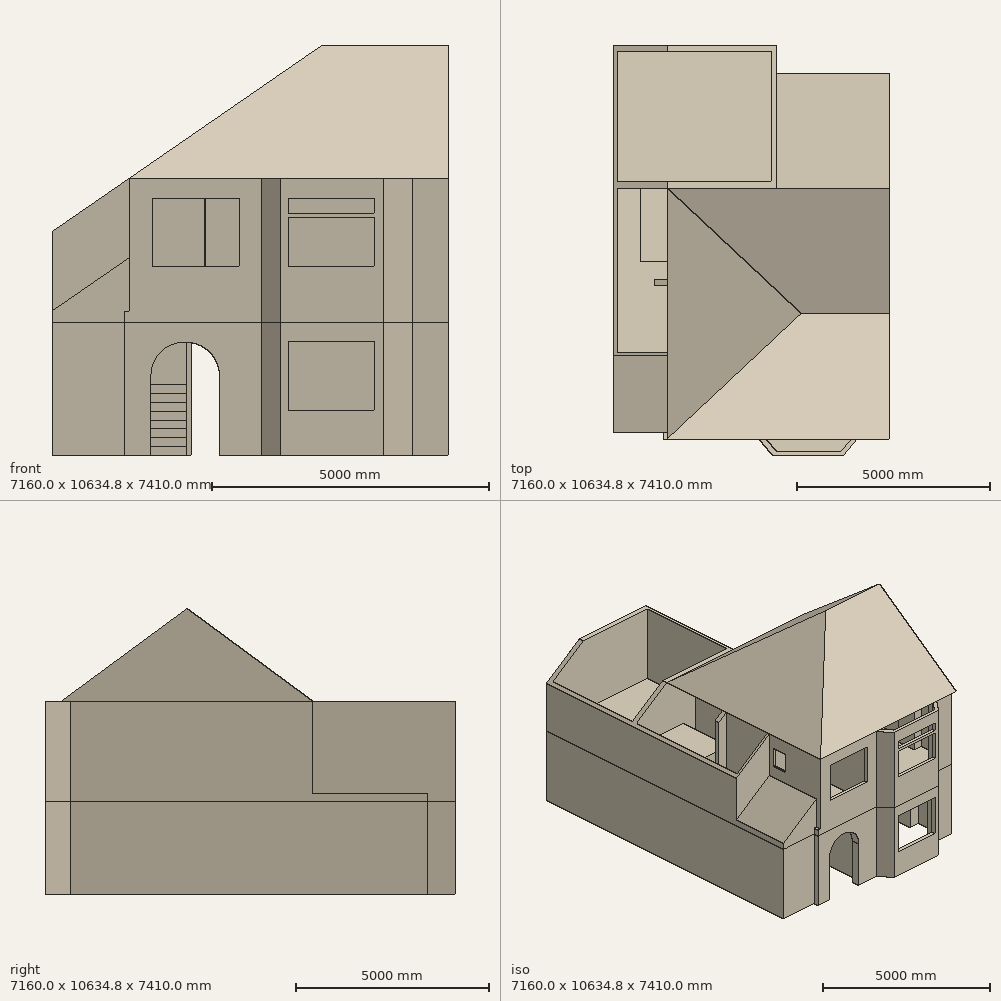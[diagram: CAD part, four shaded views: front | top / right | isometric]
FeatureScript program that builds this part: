
annotation { "Feature Type Name" : "Feature", "Feature Type Description" : "" }
export const myFeature = defineFeature(function(context is Context, id is Id, definition is map)
    precondition{}
    {
        {
            var Q0;
            Q0=qCreatedBy(makeId("Top.planeOp"),FACE);
            var sketch = newSketch(context, id + "F0", { "sketchPlane" : qUnion([Q0])});
            skLineSegment(sketch, "E0", {"start": v(2552.4, 6470.91) * mm, "end": v(2552.4, 3770.91) * mm});
            skLineSegment(sketch, "E1", {"start": v(2552.4, 2380.91) * mm, "end": v(2552.4, 1370.91) * mm});
            skLineSegment(sketch, "E2", {"start": v(2552.4, 1370.91) * mm, "end": v(-527.6, 1370.91) * mm});
            skLineSegment(sketch, "E3", {"start": v(-527.6, 2110.91) * mm, "end": v(-527.6, 1960.91) * mm});
            skLineSegment(sketch, "E4", {"start": v(-787.6, 1960.91) * mm, "end": v(-977.66, 1960.91) * mm});
            skLineSegment(sketch, "E5", {"start": v(2812.4, 6649.64) * mm, "end": v(2812.4, -1621.99) * mm});
            skLineSegment(sketch, "E6", {"start": v(-527.6, 2110.91) * mm, "end": v(-527.6, 2980.91) * mm});
            skLineSegment(sketch, "E7", {"start": v(-527.6, 2980.91) * mm, "end": v(-787.6, 2980.91) * mm});
            skLineSegment(sketch, "E8", {"start": v(-787.6, 2980.91) * mm, "end": v(-787.6, 2110.91) * mm});
            skLineSegment(sketch, "E9", {"start": v(-1127.6, -1558.17) * mm, "end": v(-1127.6, 125.16) * mm});
            skLineSegment(sketch, "E10.bottom", {"start": v(-2787.6, -689.09) * mm, "end": v(-1927.6, -689.09) * mm});
            skLineSegment(sketch, "E10.right", {"start": v(-1927.6, -689.09) * mm, "end": v(-1927.6, 1290.91) * mm});
            skLineSegment(sketch, "E11", {"start": v(-1127.6, 1033.52) * mm, "end": v(-1127.6, 692.07) * mm});
            skLineSegment(sketch, "E12", {"start": v(-1127.6, 692.07) * mm, "end": v(-977.6, 692.07) * mm});
            skLineSegment(sketch, "E13", {"start": v(-977.6, 692.07) * mm, "end": v(-977.6, 971.05) * mm});
            skLineSegment(sketch, "E14", {"start": v(-488.3, 1220.91) * mm, "end": v(2552.4, 1220.91) * mm});
            skLineSegment(sketch, "E15", {"start": v(2552.4, 1220.91) * mm, "end": v(2552.4, 220.91) * mm});
            skLineSegment(sketch, "E16", {"start": v(2552.4, 220.91) * mm, "end": v(2202.4, 220.91) * mm});
            skLineSegment(sketch, "E17", {"start": v(2202.4, 220.91) * mm, "end": v(2202.4, -488.25) * mm});
            skLineSegment(sketch, "E18", {"start": v(2202.4, -488.25) * mm, "end": v(2552.4, -488.25) * mm});
            skLineSegment(sketch, "E19", {"start": v(2552.4, -488.25) * mm, "end": v(2552.4, -1478.25) * mm});
            skLineSegment(sketch, "E20", {"start": v(2552.4, -1478.25) * mm, "end": v(1962.4, -1478.25) * mm});
            skLineSegment(sketch, "E21", {"start": v(1962.4, -1478.25) * mm, "end": v(1962.4, -1678.25) * mm});
            skLineSegment(sketch, "E22", {"start": v(1962.4, -1678.25) * mm, "end": v(1571.93, -2133.8) * mm});
            skLineSegment(sketch, "E23", {"start": v(1571.93, -2133.8) * mm, "end": v(-88.07, -2133.8) * mm});
            skLineSegment(sketch, "E24", {"start": v(-88.07, -2133.8) * mm, "end": v(-497.46, -1695.17) * mm});
            skLineSegment(sketch, "E25", {"start": v(2812.4, -1621.99) * mm, "end": v(2157.57, -1621.99) * mm});
            skLineSegment(sketch, "E26", {"start": v(2157.57, -1621.99) * mm, "end": v(1628.97, -2263.86) * mm});
            skLineSegment(sketch, "E27", {"start": v(1628.97, -2263.86) * mm, "end": v(-224.9, -2263.86) * mm});
            skLineSegment(sketch, "E28", {"start": v(-224.9, -2263.86) * mm, "end": v(-574.97, -1840.1) * mm});
            skLineSegment(sketch, "E29", {"start": v(-574.97, -1840.1) * mm, "end": v(-1127.6, -1840.1) * mm});
            skLineSegment(sketch, "E30", {"start": v(-977.6, -1684.67) * mm, "end": v(-497.46, -1695.17) * mm});
            skPoint(sketch, "E31.orphan", {"position": v(2812.4, -2479.09) * mm});
            skLineSegment(sketch, "E32", {"start": v(-1127.6, 125.16) * mm, "end": v(-977.6, 125.16) * mm});
            skLineSegment(sketch, "E33", {"start": v(-977.6, 125.16) * mm, "end": v(-977.6, -1684.67) * mm});
            skLineSegment(sketch, "E34", {"start": v(-1127.6, 1033.52) * mm, "end": v(-787.6, 1370.91) * mm});
            skLineSegment(sketch, "E35", {"start": v(-977.6, 971.05) * mm, "end": v(-725.8, 1220.91) * mm});
            skLineSegment(sketch, "E36", {"start": v(-488.3, 1220.91) * mm, "end": v(-725.8, 1220.91) * mm});
            skLineSegment(sketch, "E37", {"start": v(-1927.6, 1960.91) * mm, "end": v(-1927.6, 1890.91) * mm});
            skLineSegment(sketch, "E38", {"start": v(-3047.6, -1674.58) * mm, "end": v(-4347.6, -1674.58) * mm});
            skLineSegment(sketch, "E39", {"start": v(-4347.6, -1674.58) * mm, "end": v(-4347.6, 8370.91) * mm});
            skLineSegment(sketch, "E40", {"start": v(-4347.6, 8370.91) * mm, "end": v(-3782.36, 8370.91) * mm});
            skLineSegment(sketch, "E41", {"start": v(-5107.6, 9981.54) * mm, "end": v(-5107.6, -3919.8) * mm});
            skLineSegment(sketch, "E42", {"start": v(-527.6, 1960.91) * mm, "end": v(-527.6, 1370.91) * mm});
            skLineSegment(sketch, "E43", {"start": v(-787.6, 2110.91) * mm, "end": v(-787.6, 1370.91) * mm});
            skLineSegment(sketch, "E44", {"start": v(-1841.48, 2110.91) * mm, "end": v(-1841.48, 1960.91) * mm});
            skLineSegment(sketch, "E45", {"start": v(-977.66, 2110.91) * mm, "end": v(-977.66, 1960.91) * mm});
            skLineSegment(sketch, "E46.trimOffspring", {"start": v(-977.66, 2110.91) * mm, "end": v(-787.6, 2110.91) * mm});
            skLineSegment(sketch, "E47", {"start": v(-4047.6, 2980.91) * mm, "end": v(-4047.6, 8103.1) * mm});
            skLineSegment(sketch, "E48", {"start": v(-4047.6, 8103.1) * mm, "end": v(-3782.36, 8103.1) * mm});
            skLineSegment(sketch, "E49", {"start": v(-3782.36, 8103.1) * mm, "end": v(-3782.36, 8370.91) * mm});
            skLineSegment(sketch, "E50", {"start": v(-4047.6, 525.28) * mm, "end": v(-3047.6, 525.28) * mm});
            skLineSegment(sketch, "E51", {"start": v(-3047.6, 525.28) * mm, "end": v(-2787.6, 525.28) * mm});
            skLineSegment(sketch, "E52", {"start": v(-2787.6, 525.28) * mm, "end": v(-2787.6, 1290.91) * mm});
            skLineSegment(sketch, "E53", {"start": v(-1927.6, 1290.91) * mm, "end": v(-2787.6, 1290.91) * mm});
            skLineSegment(sketch, "E54", {"start": v(-2787.6, 1290.91) * mm, "end": v(-3047.6, 1290.91) * mm});
            skLineSegment(sketch, "E55.trimOffspring", {"start": v(-3047.6, 1290.91) * mm, "end": v(-3047.6, 525.28) * mm});
            skLineSegment(sketch, "E56.trimOffspring", {"start": v(-1927.6, 1890.91) * mm, "end": v(-1927.6, 1960.91) * mm});
            skLineSegment(sketch, "E57", {"start": v(-126.84, 8370.91) * mm, "end": v(-126.84, 7649.64) * mm});
            skLineSegment(sketch, "E58", {"start": v(-126.84, 7649.64) * mm, "end": v(2812.4, 7649.64) * mm});
            skLineSegment(sketch, "E59", {"start": v(2812.4, 7649.64) * mm, "end": v(2812.4, 6649.64) * mm});
            skLineSegment(sketch, "E60", {"start": v(2552.4, 6470.91) * mm, "end": v(2552.4, 7649.64) * mm});
            skLineSegment(sketch, "E61.bottom", {"start": v(-563.87, 8370.91) * mm, "end": v(-126.84, 8370.91) * mm});
            skLineSegment(sketch, "E61.top", {"start": v(-563.87, 8103.1) * mm, "end": v(-338.1, 8103.1) * mm});
            skLineSegment(sketch, "E61.left", {"start": v(-563.87, 8370.91) * mm, "end": v(-563.87, 8103.1) * mm});
            skLineSegment(sketch, "E61.right", {"start": v(-126.84, 8370.91) * mm, "end": v(-126.84, 8103.1) * mm});
            skLineSegment(sketch, "E62.bottom", {"start": v(-3047.6, -859.72) * mm, "end": v(-2787.6, -859.72) * mm});
            skLineSegment(sketch, "E62.top", {"start": v(-3047.6, -1558.17) * mm, "end": v(-2787.6, -1558.17) * mm});
            skLineSegment(sketch, "E63.trimOffspring", {"start": v(-3047.6, -1674.58) * mm, "end": v(-3047.6, -1840.1) * mm});
            skLineSegment(sketch, "E64.trimOffspring", {"start": v(-2787.6, -859.72) * mm, "end": v(-2787.6, 1290.91) * mm});
            skLineSegment(sketch, "E65", {"start": v(-3047.6, -1558.17) * mm, "end": v(-4047.6, -1558.17) * mm});
            skLineSegment(sketch, "E66", {"start": v(-4047.6, 525.28) * mm, "end": v(-4047.6, -1558.17) * mm});
            skLineSegment(sketch, "E67", {"start": v(2552.4, 7349.64) * mm, "end": v(-338.1, 7349.64) * mm});
            skLineSegment(sketch, "E68", {"start": v(-338.1, 7349.64) * mm, "end": v(-338.1, 8103.1) * mm});
            skLineSegment(sketch, "E69", {"start": v(2552.4, 3770.91) * mm, "end": v(2552.4, 2980.91) * mm});
            skLineSegment(sketch, "E70", {"start": v(0, 7349.64) * mm, "end": v(0, 5540.32) * mm, "construction": true});
            skLineSegment(sketch, "E71", {"start": v(0, 5540.32) * mm, "end": v(679.13, 5540.32) * mm, "construction": true});
            skLineSegment(sketch, "E72", {"start": v(679.13, 5540.32) * mm, "end": v(679.13, 7349.64) * mm, "construction": true});
            skLineSegment(sketch, "E73", {"start": v(2552.4, 4248.58) * mm, "end": v(816.18, 4248.58) * mm});
            skLineSegment(sketch, "E74", {"start": v(816.18, 4248.58) * mm, "end": v(816.18, 3608.36) * mm, "construction": true});
            skLineSegment(sketch, "E75", {"start": v(816.18, 3608.36) * mm, "end": v(2552.4, 3608.36) * mm, "construction": true});
            skLineSegment(sketch, "E76", {"start": v(-1127.6, -1840.1) * mm, "end": v(-3047.6, -1840.1) * mm});
            skLineSegment(sketch, "E77", {"start": v(-2787.6, -1558.17) * mm, "end": v(-2738.72, -1558.17) * mm});
            skLineSegment(sketch, "E78", {"start": v(-1127.6, -1558.17) * mm, "end": v(-2787.6, -1558.17) * mm});
            skLineSegment(sketch, "E79", {"start": v(1952.4, 7349.64) * mm, "end": v(1952.4, 4248.58) * mm, "construction": true});
            skLineSegment(sketch, "E80", {"start": v(-3047.6, -859.72) * mm, "end": v(-3047.6, 1290.91) * mm});
            skLineSegment(sketch, "E81.trimOffspring", {"start": v(679.13, 6634.48) * mm, "end": v(0, 6628.99) * mm});
            skLineSegment(sketch, "E82", {"start": v(1952.4, 6749.64) * mm, "end": v(679.13, 6749.64) * mm, "construction": true});
            skLineSegment(sketch, "E83", {"start": v(-4047.6, 2980.91) * mm, "end": v(-1841.48, 2980.91) * mm});
            skLineSegment(sketch, "E84", {"start": v(-1841.48, 2980.91) * mm, "end": v(-1841.48, 2110.91) * mm});
            skLineSegment(sketch, "E85", {"start": v(364.1, 2980.91) * mm, "end": v(2552.4, 2980.91) * mm});
            skPoint(sketch, "E86.start.orphan", {"position": v(-4047.6, 1960.91) * mm});
            skPoint(sketch, "E87.orphan", {"position": v(-4047.6, 2110.91) * mm});
            skLineSegment(sketch, "E88", {"start": v(-4047.6, 2980.91) * mm, "end": v(-4047.6, 525.28) * mm});
            skLineSegment(sketch, "E89", {"start": v(364.1, 2883.99) * mm, "end": v(2552.4, 2883.99) * mm});
            skLineSegment(sketch, "E90", {"start": v(-1927.6, 1960.91) * mm, "end": v(-1927.6, 2896.75) * mm});
            skLineSegment(sketch, "E91", {"start": v(-1927.6, 2896.75) * mm, "end": v(-4047.6, 2896.75) * mm});
            skLineSegment(sketch, "E92", {"start": v(-1841.48, 1960.91) * mm, "end": v(-1841.48, 1890.91) * mm});
            skLineSegment(sketch, "E93", {"start": v(-1841.48, 1890.91) * mm, "end": v(-1927.6, 1890.91) * mm});
            skLineSegment(sketch, "E94", {"start": v(-527.6, 2883.99) * mm, "end": v(-527.6, 2980.91) * mm});
            skLineSegment(sketch, "E95", {"start": v(364.1, 2883.99) * mm, "end": v(364.1, 2980.91) * mm});
            skLineSegment(sketch, "E96.trimOffspring", {"start": v(2552.4, 2883.99) * mm, "end": v(2552.4, 2380.91) * mm});
            skSolve(sketch);
        }
        {
            var Q0;
            {var subQ6=sQuery(id+"F0.wireOp",EDGE,"E1");Q0=makeQuery(id+"F0.imprint","IMPRINT",FACE,{"disambiguationData":[TD([[makeQuery(id+"F0.imprint","IMPRINT",EDGE,{"derivedFrom":subQ6}),1.0]])]});}
            var sketch = newSketch(context, id + "F1", { "sketchPlane" : qUnion([Q0])});
            skLineSegment(sketch, "E97.bottom", {"start": v(0, 7357.64) * mm, "end": v(691.93, 7357.64) * mm});
            skLineSegment(sketch, "E97.top", {"start": v(0, 5513.83) * mm, "end": v(691.93, 5513.83) * mm});
            skLineSegment(sketch, "E97.left", {"start": v(0, 7357.64) * mm, "end": v(0, 5513.83) * mm});
            skLineSegment(sketch, "E97.right", {"start": v(691.93, 7357.64) * mm, "end": v(691.93, 5513.83) * mm});
            skLineSegment(sketch, "E98.bottom", {"start": v(691.93, 6686.96) * mm, "end": v(2496.44, 6686.96) * mm});
            skLineSegment(sketch, "E98.top", {"start": v(691.93, 7229.15) * mm, "end": v(2496.44, 7229.15) * mm});
            skLineSegment(sketch, "E98.left", {"start": v(691.93, 6686.96) * mm, "end": v(691.93, 7229.15) * mm});
            skLineSegment(sketch, "E98.right", {"start": v(2496.44, 6686.96) * mm, "end": v(2496.44, 7229.15) * mm});
            skLineSegment(sketch, "E99.bottom", {"start": v(1974.66, 6686.96) * mm, "end": v(2491.44, 6686.96) * mm});
            skLineSegment(sketch, "E99.top", {"start": v(1974.66, 4299.47) * mm, "end": v(2491.44, 4299.47) * mm});
            skLineSegment(sketch, "E99.left", {"start": v(1974.66, 6686.96) * mm, "end": v(1974.66, 4299.47) * mm});
            skLineSegment(sketch, "E99.right", {"start": v(2491.44, 6686.96) * mm, "end": v(2491.44, 4299.47) * mm});
            skLineSegment(sketch, "E100.bottom", {"start": v(868.55, 4244.74) * mm, "end": v(2505.25, 4244.74) * mm});
            skLineSegment(sketch, "E100.top", {"start": v(868.55, 3653.24) * mm, "end": v(2505.25, 3653.24) * mm});
            skLineSegment(sketch, "E100.left", {"start": v(868.55, 4244.74) * mm, "end": v(868.55, 3653.24) * mm});
            skLineSegment(sketch, "E100.right", {"start": v(2505.25, 4244.74) * mm, "end": v(2505.25, 3653.24) * mm});
            skSolve(sketch);
        }
        {
            var Q0;
            Q0=makeQuery(id+"F0.imprint","IMPRINT",FACE,{"disambiguationData":[TD([[makeQuery(id+"F0.imprint","IMPRINT",EDGE,{"derivedFrom":sQuery(id+"F0.wireOp",EDGE,"E1")}),1.0]])]});
            var Q1;
            {var subQ2=sQuery(id+"F0.wireOp",EDGE,"E57");Q1=makeQuery(id+"F0.imprint","IMPRINT",FACE,{"disambiguationData":[TD([[makeQuery(id+"F0.imprint","IMPRINT",EDGE,{"derivedFrom":subQ2}),-1.0]])]});}
            var Q2;
            Q2=makeQuery(id+"F0.imprint","IMPRINT",FACE,{"disambiguationData":[TD([[makeQuery(id+"F0.imprint","IMPRINT",EDGE,{"derivedFrom":sQuery(id+"F0.wireOp",EDGE,"E44")}),-1.0]])]});
            extrude(context, id + "F2", {"entities" : qUnion([Q0, Q1, Q2]), "depth" : 2400 * mm});
        }
        {
            var Q0;
            Q0=makeQuery(id+"F2.opExtrude","SWEPT_FACE",FACE,{"disambiguationData":[OSD([sQuery(id+"F0.wireOp",EDGE,"E27")])]});
            var sketch = newSketch(context, id + "F3", { "sketchPlane" : qUnion([Q0])});
            skLineSegment(sketch, "E101.top", {"start": v(-74.9, 811.9) * mm, "end": v(1478.97, 811.9) * mm});
            skLineSegment(sketch, "E101.right", {"start": v(1478.97, 2052.8) * mm, "end": v(1478.97, 811.9) * mm});
            skLineSegment(sketch, "E102", {"start": v(-74.9, 2052.8) * mm, "end": v(-74.9, 802.64) * mm});
            skLineSegment(sketch, "E103", {"start": v(-74.9, 2052.8) * mm, "end": v(1478.97, 2052.8) * mm});
            skSolve(sketch);
        }
        {
            var Q0;
            Q0 = qSketchRegion(id + "F3", true);
            extrude(context, id + "F4", {"entities" : qUnion([Q0]), "operationType" : NewBodyOperationType.REMOVE, "oppositeDirection" : true, "depth" : 947.03 * mm});
        }
        {
            var Q0;
            Q0=makeQuery(id+"F2.opExtrude","SWEPT_FACE",FACE,{"disambiguationData":[OSD([sQuery(id+"F0.wireOp",EDGE,"E58")])]});
            var sketch = newSketch(context, id + "F5", { "sketchPlane" : qUnion([Q0])});
            skLineSegment(sketch, "E104.bottom", {"start": v(-2335.52, 1864.67) * mm, "end": v(-597.18, 1864.67) * mm});
            skLineSegment(sketch, "E104.top", {"start": v(-2335.52, 836.66) * mm, "end": v(-597.18, 836.66) * mm});
            skLineSegment(sketch, "E104.left", {"start": v(-2335.52, 1864.67) * mm, "end": v(-2335.52, 836.66) * mm});
            skLineSegment(sketch, "E104.right", {"start": v(-597.18, 1864.67) * mm, "end": v(-597.18, 836.66) * mm});
            skSolve(sketch);
        }
        {
            var Q0;
            Q0=makeQuery(id+"F5.imprint","IMPRINT",FACE,{"disambiguationData":[TD([[makeQuery(id+"F5.imprint","IMPRINT",EDGE,{"derivedFrom":sQuery(id+"F5.wireOp",EDGE,"E104.bottom")}),-1.0]])]});
            extrude(context, id + "F6", {"entities" : qUnion([Q0]), "operationType" : NewBodyOperationType.REMOVE, "oppositeDirection" : true, "depth" : 1716.48 * mm});
        }
        {
            var Q0;
            Q0=makeQuery(id+"F2.opExtrude","SWEPT_FACE",FACE,{"disambiguationData":[OSD([sQuery(id+"F0.wireOp",EDGE,"E38")])]});
            var sketch = newSketch(context, id + "F7", { "sketchPlane" : qUnion([Q0])});
            skLineSegment(sketch, "E105", {"start": v(-2567.6, 0) * mm, "end": v(-2567.6, 1430) * mm});
            skLineSegment(sketch, "E106", {"start": v(-1327.6, 0) * mm, "end": v(-1327.6, 1430) * mm});
            skArc(sketch, "E107", {"start": v(-1327.6, 1430) * mm, "mid": v(-1947.6, 2050) * mm, "end": v(-2567.6, 1430) * mm});
            skLineSegment(sketch, "E108", {"start": v(-2567.6, 0) * mm, "end": v(-1327.6, 0) * mm});
            skSolve(sketch);
        }
        {
            var Q0;
            Q0 = qSketchRegion(id + "F7", true);
            extrude(context, id + "F8", {"entities" : qUnion([Q0]), "operationType" : NewBodyOperationType.REMOVE, "depth" : 948.33 * mm});
        }
        {
            var Q0;
            Q0=makeQuery(id+"F8.boolean.opBoolean","COPY",FACE,{"derivedFrom":makeQuery(id+"F8.opExtrude","CAP_FACE",FACE,{"disambiguationData":[OSD([sQuery(id+"F7.wireOp",EDGE,"E105"),sQuery(id+"F7.wireOp",EDGE,"E106"),sQuery(id+"F7.wireOp",EDGE,"E107"),sQuery(id+"F7.wireOp",EDGE,"E108")])],"isStart":true})});
            extrude(context, id + "F9", {"entities" : qUnion([Q0]), "operationType" : NewBodyOperationType.REMOVE, "oppositeDirection" : true, "depth" : 366.27 * mm});
        }
        {
            var Q0;
            {var subQ2=sQuery(id+"F0.wireOp",EDGE,"E51");Q0=makeQuery(id+"F0.imprint","IMPRINT",FACE,{"disambiguationData":[TD([[makeQuery(id+"F0.imprint","IMPRINT",EDGE,{"derivedFrom":subQ2}),-1.0]])]});}
            var Q1;
            {var subQ2=sQuery(id+"F0.wireOp",EDGE,"E51");Q1=makeQuery(id+"F0.imprint","IMPRINT",FACE,{"disambiguationData":[TD([[makeQuery(id+"F0.imprint","IMPRINT",EDGE,{"derivedFrom":subQ2}),1.0]])]});}
            var Q2;
            {var subQ3=sQuery(id+"F0.wireOp",EDGE,"E10.bottom");Q2=makeQuery(id+"F0.imprint","IMPRINT",FACE,{"disambiguationData":[TD([[makeQuery(id+"F0.imprint","IMPRINT",EDGE,{"derivedFrom":subQ3}),1.0]])]});}
            extrude(context, id + "F10", {"entities" : qUnion([Q0, Q1, Q2]), "depth" : 2400 * mm});
        }
        {
            var Q0;
            Q0=makeQuery(id+"F10.opExtrude","SWEPT_FACE",FACE,{"disambiguationData":[OSD([sQuery(id+"F0.wireOp",EDGE,"E10.right")])]});
            var sketch = newSketch(context, id + "F11", { "sketchPlane" : qUnion([Q0])});
            skLineSegment(sketch, "E109", {"start": v(-689.09, 160) * mm, "end": v(-529.09, 160) * mm});
            skLineSegment(sketch, "E110", {"start": v(-529.09, 160) * mm, "end": v(-529.09, 320) * mm});
            skLineSegment(sketch, "E111", {"start": v(-529.09, 320) * mm, "end": v(-369.09, 320) * mm});
            skLineSegment(sketch, "E112", {"start": v(-369.09, 320) * mm, "end": v(-369.09, 480) * mm});
            skLineSegment(sketch, "E113", {"start": v(-369.09, 480) * mm, "end": v(-209.09, 480) * mm});
            skLineSegment(sketch, "E114", {"start": v(-209.09, 480) * mm, "end": v(-209.09, 640) * mm});
            skLineSegment(sketch, "E115", {"start": v(-209.09, 640) * mm, "end": v(-49.09, 640) * mm});
            skLineSegment(sketch, "E116", {"start": v(-49.09, 640) * mm, "end": v(-49.09, 800) * mm});
            skLineSegment(sketch, "E117", {"start": v(-49.09, 800) * mm, "end": v(110.91, 800) * mm});
            skLineSegment(sketch, "E118", {"start": v(110.91, 800) * mm, "end": v(110.91, 960) * mm});
            skLineSegment(sketch, "E119", {"start": v(110.91, 960) * mm, "end": v(270.91, 960) * mm});
            skLineSegment(sketch, "E120", {"start": v(270.91, 960) * mm, "end": v(270.91, 1120) * mm});
            skLineSegment(sketch, "E121", {"start": v(270.91, 1120) * mm, "end": v(430.91, 1120) * mm});
            skLineSegment(sketch, "E122", {"start": v(430.91, 1120) * mm, "end": v(430.91, 1280) * mm});
            skLineSegment(sketch, "E123", {"start": v(430.91, 1280) * mm, "end": v(597.6, 1280) * mm});
            skLineSegment(sketch, "E124", {"start": v(597.6, 1280) * mm, "end": v(1290.91, 1280) * mm});
            skLineSegment(sketch, "E125", {"start": v(-689.09, 160) * mm, "end": v(-689.09, 0) * mm});
            skLineSegment(sketch, "E126", {"start": v(-689.09, 0) * mm, "end": v(1290.91, 0) * mm});
            skLineSegment(sketch, "E127", {"start": v(1290.91, 0) * mm, "end": v(1290.91, 1280) * mm});
            skSolve(sketch);
        }
        {
            var Q0;
            {var subQ5=sQuery(id+"F11.wireOp",EDGE,"E109");Q0=makeQuery(id+"F11.imprint","IMPRINT",FACE,{"disambiguationData":[TD([[makeQuery(id+"F11.imprint","IMPRINT",EDGE,{"derivedFrom":subQ5}),1.0]])]});}
            var Q1;
            Q1=makeQuery(id+"F10.opExtrude","SWEPT_FACE",FACE,{"disambiguationData":[OSD([sQuery(id+"F0.wireOp",EDGE,"E64.trimOffspring")])]});
            extrude(context, id + "F12", {"entities" : qUnion([Q0]), "operationType" : NewBodyOperationType.REMOVE, "endBound" : BoundingType.UP_TO_SURFACE, "oppositeDirection" : true, "endBoundEntityFace" : qUnion([Q1]), "depth" : 329.84 * mm});
        }
        {
            var Q0;
            Q0=makeQuery(id+"F2.opExtrude","CAP_FACE",FACE,{"disambiguationData":[OSD([sQuery(id+"F0.wireOp",EDGE,"E0"),sQuery(id+"F0.wireOp",EDGE,"E1"),sQuery(id+"F0.wireOp",EDGE,"53525224-3efd-418c-8780-7c12f9d2bcd3"),sQuery(id+"F0.wireOp",EDGE,"E3"),sQuery(id+"F0.wireOp",EDGE,"E4"),sQuery(id+"F0.wireOp",EDGE,"E5"),sQuery(id+"F0.wireOp",EDGE,"E6"),sQuery(id+"F0.wireOp",EDGE,"E7"),sQuery(id+"F0.wireOp",EDGE,"E8"),sQuery(id+"F0.wireOp",EDGE,"E9"),sQuery(id+"F0.wireOp",EDGE,"E11"),sQuery(id+"F0.wireOp",EDGE,"E12"),sQuery(id+"F0.wireOp",EDGE,"E13"),sQuery(id+"F0.wireOp",EDGE,"E14"),sQuery(id+"F0.wireOp",EDGE,"E15"),sQuery(id+"F0.wireOp",EDGE,"E16"),sQuery(id+"F0.wireOp",EDGE,"E17"),sQuery(id+"F0.wireOp",EDGE,"E18"),sQuery(id+"F0.wireOp",EDGE,"E19"),sQuery(id+"F0.wireOp",EDGE,"E20"),sQuery(id+"F0.wireOp",EDGE,"E21"),sQuery(id+"F0.wireOp",EDGE,"E22"),sQuery(id+"F0.wireOp",EDGE,"E23"),sQuery(id+"F0.wireOp",EDGE,"E24"),sQuery(id+"F0.wireOp",EDGE,"E25"),sQuery(id+"F0.wireOp",EDGE,"E26"),sQuery(id+"F0.wireOp",EDGE,"E27"),sQuery(id+"F0.wireOp",EDGE,"E28"),sQuery(id+"F0.wireOp",EDGE,"E29"),sQuery(id+"F0.wireOp",EDGE,"E30"),sQuery(id+"F0.wireOp",EDGE,"E32"),sQuery(id+"F0.wireOp",EDGE,"E33"),sQuery(id+"F0.wireOp",EDGE,"E2"),sQuery(id+"F0.wireOp",EDGE,"E34"),sQuery(id+"F0.wireOp",EDGE,"E35"),sQuery(id+"F0.wireOp",EDGE,"E36"),sQuery(id+"F0.wireOp",EDGE,"E38"),sQuery(id+"F0.wireOp",EDGE,"E39"),sQuery(id+"F0.wireOp",EDGE,"E40"),sQuery(id+"F0.wireOp",EDGE,"E42"),sQuery(id+"F0.wireOp",EDGE,"E43"),sQuery(id+"F0.wireOp",EDGE,"E44"),sQuery(id+"F0.wireOp",EDGE,"E45"),sQuery(id+"F0.wireOp",EDGE,"E46.trimOffspring"),sQuery(id+"F0.wireOp",EDGE,"9fa25718-6e3d-4a3c-a5d5-3a83e1431973"),sQuery(id+"F0.wireOp",EDGE,"E47"),sQuery(id+"F0.wireOp",EDGE,"E48"),sQuery(id+"F0.wireOp",EDGE,"E49"),sQuery(id+"F0.wireOp",EDGE,"E86"),sQuery(id+"F0.wireOp",EDGE,"a6f443fb-dac8-401c-8383-66d9b94825dd"),sQuery(id+"F0.wireOp",EDGE,"E57"),sQuery(id+"F0.wireOp",EDGE,"E58"),sQuery(id+"F0.wireOp",EDGE,"E59"),sQuery(id+"F0.wireOp",EDGE,"E60"),sQuery(id+"F0.wireOp",EDGE,"E61.top"),sQuery(id+"F0.wireOp",EDGE,"E61.left"),sQuery(id+"F0.wireOp",EDGE,"E61.right"),sQuery(id+"F0.wireOp",EDGE,"E61.bottom"),sQuery(id+"F0.wireOp",EDGE,"E62.top"),sQuery(id+"F0.wireOp",EDGE,"E63.trimOffspring"),sQuery(id+"F0.wireOp",EDGE,"E65"),sQuery(id+"F0.wireOp",EDGE,"E66"),sQuery(id+"F0.wireOp",EDGE,"E67"),sQuery(id+"F0.wireOp",EDGE,"E68"),sQuery(id+"F0.wireOp",EDGE,"E69"),sQuery(id+"F0.wireOp",EDGE,"E76"),sQuery(id+"F0.wireOp",EDGE,"E78")])],"isStart":false});
            var sketch = newSketch(context, id + "F13", { "sketchPlane" : qUnion([Q0])});
            skLineSegment(sketch, "E128", {"start": v(-126.84, 8370.91) * mm, "end": v(-4347.6, 8370.91) * mm});
            skLineSegment(sketch, "E129", {"start": v(-4347.6, 8370.91) * mm, "end": v(-4347.6, -1674.58) * mm});
            skLineSegment(sketch, "E130", {"start": v(-4347.6, -1674.58) * mm, "end": v(-3047.6, -1674.58) * mm});
            skLineSegment(sketch, "E131", {"start": v(-3047.6, -1674.58) * mm, "end": v(-3047.6, -1840.1) * mm});
            skLineSegment(sketch, "E132", {"start": v(-3047.6, -1840.1) * mm, "end": v(-574.97, -1840.1) * mm});
            skLineSegment(sketch, "E133", {"start": v(-574.97, -1840.1) * mm, "end": v(-224.9, -2263.86) * mm});
            skLineSegment(sketch, "E134", {"start": v(-224.9, -2263.86) * mm, "end": v(1628.97, -2263.86) * mm});
            skLineSegment(sketch, "E135", {"start": v(1628.97, -2263.86) * mm, "end": v(2157.57, -1621.99) * mm});
            skLineSegment(sketch, "E136", {"start": v(2157.57, -1621.99) * mm, "end": v(2812.4, -1621.99) * mm});
            skLineSegment(sketch, "E137", {"start": v(2812.4, -1621.99) * mm, "end": v(2812.4, 7649.64) * mm});
            skLineSegment(sketch, "E138", {"start": v(2812.4, 7649.64) * mm, "end": v(-126.84, 7649.64) * mm});
            skLineSegment(sketch, "E139", {"start": v(-126.84, 7649.64) * mm, "end": v(-126.84, 8370.91) * mm});
            skSolve(sketch);
        }
        {
            var Q0;
            Q0 = qSketchRegion(id + "F13", true);
            extrude(context, id + "F14", {"entities" : qUnion([Q0]), "depth" : 210 * mm});
        }
        {
            var Q0;
            Q0=makeQuery(id+"F14.opExtrude","CAP_FACE",FACE,{"disambiguationData":[OSD([sQuery(id+"F13.wireOp",EDGE,"E128"),sQuery(id+"F13.wireOp",EDGE,"E129"),sQuery(id+"F13.wireOp",EDGE,"E130"),sQuery(id+"F13.wireOp",EDGE,"E131"),sQuery(id+"F13.wireOp",EDGE,"E132"),sQuery(id+"F13.wireOp",EDGE,"E133"),sQuery(id+"F13.wireOp",EDGE,"E134"),sQuery(id+"F13.wireOp",EDGE,"E135"),sQuery(id+"F13.wireOp",EDGE,"E136"),sQuery(id+"F13.wireOp",EDGE,"E137"),sQuery(id+"F13.wireOp",EDGE,"E138"),sQuery(id+"F13.wireOp",EDGE,"E139")])],"isStart":false});
            var sketch = newSketch(context, id + "F15", { "sketchPlane" : qUnion([Q0])});
            skLineSegment(sketch, "E140.bottom", {"start": v(-1924.03, 402.37) * mm, "end": v(-2761.06, 402.37) * mm});
            skLineSegment(sketch, "E140.top", {"start": v(-1924.03, 1956.01) * mm, "end": v(-2761.06, 1956.01) * mm});
            skLineSegment(sketch, "E140.left", {"start": v(-1924.03, 402.37) * mm, "end": v(-1924.03, 1272.66) * mm});
            skLineSegment(sketch, "E140.right", {"start": v(-2761.06, 402.37) * mm, "end": v(-2761.06, 1956.01) * mm});
            skLineSegment(sketch, "E141", {"start": v(-1924.03, 1956.01) * mm, "end": v(-1690.6, 1956.01) * mm});
            skLineSegment(sketch, "E142", {"start": v(-1690.6, 1956.01) * mm, "end": v(-1690.6, 1272.66) * mm});
            skLineSegment(sketch, "E143", {"start": v(-1690.6, 1272.66) * mm, "end": v(-1924.03, 1272.66) * mm});
            skSolve(sketch);
        }
        {
            var Q0;
            Q0=makeQuery(id+"F15.imprint","IMPRINT",FACE,{"disambiguationData":[TD([[makeQuery(id+"F15.imprint","IMPRINT",EDGE,{"derivedFrom":sQuery(id+"F15.wireOp",EDGE,"E140.bottom")}),-1.0]])]});
            extrude(context, id + "F16", {"entities" : qUnion([Q0]), "operationType" : NewBodyOperationType.REMOVE, "oppositeDirection" : true, "depth" : 244.46 * mm});
        }
        {
            var Q0;
            Q0=makeQuery(id+"F14.opExtrude","CAP_FACE",FACE,{"disambiguationData":[OSD([sQuery(id+"F13.wireOp",EDGE,"E128"),sQuery(id+"F13.wireOp",EDGE,"E129"),sQuery(id+"F13.wireOp",EDGE,"E130"),sQuery(id+"F13.wireOp",EDGE,"E131"),sQuery(id+"F13.wireOp",EDGE,"E132"),sQuery(id+"F13.wireOp",EDGE,"E133"),sQuery(id+"F13.wireOp",EDGE,"E134"),sQuery(id+"F13.wireOp",EDGE,"E135"),sQuery(id+"F13.wireOp",EDGE,"E136"),sQuery(id+"F13.wireOp",EDGE,"E137"),sQuery(id+"F13.wireOp",EDGE,"E138"),sQuery(id+"F13.wireOp",EDGE,"E139")])],"isStart":false});
            var sketch = newSketch(context, id + "F17", { "sketchPlane" : qUnion([Q0])});
            skLineSegment(sketch, "E144", {"start": v(-126.84, 8370.91) * mm, "end": v(-126.84, 4670.91) * mm});
            skLineSegment(sketch, "E145", {"start": v(-126.84, 4670.91) * mm, "end": v(2812.4, 4670.91) * mm});
            skLineSegment(sketch, "E146", {"start": v(2812.4, 4670.91) * mm, "end": v(2812.4, -1621.99) * mm});
            skLineSegment(sketch, "E147", {"start": v(2812.4, -1621.99) * mm, "end": v(2157.57, -1621.99) * mm});
            skLineSegment(sketch, "E148", {"start": v(2157.57, -1621.99) * mm, "end": v(1628.97, -2263.86) * mm});
            skLineSegment(sketch, "E149", {"start": v(1628.97, -2263.86) * mm, "end": v(-224.9, -2263.86) * mm});
            skLineSegment(sketch, "E150", {"start": v(-224.9, -2263.86) * mm, "end": v(-574.97, -1840.1) * mm});
            skLineSegment(sketch, "E151", {"start": v(-574.97, -1840.1) * mm, "end": v(-2948.68, -1840.1) * mm});
            skLineSegment(sketch, "E152", {"start": v(-4347.6, 319.79) * mm, "end": v(-4347.6, 8370.91) * mm});
            skLineSegment(sketch, "E153", {"start": v(-4347.6, 8370.91) * mm, "end": v(-126.84, 8370.91) * mm});
            skLineSegment(sketch, "E154", {"start": v(-2948.68, -1529.24) * mm, "end": v(-2948.68, -1724.11) * mm});
            skLineSegment(sketch, "E155", {"start": v(-822.49, -1724.11) * mm, "end": v(-822.49, 436.6) * mm});
            skLineSegment(sketch, "E156", {"start": v(-822.49, 1403.85) * mm, "end": v(-822.49, 1223.05) * mm});
            skLineSegment(sketch, "E157", {"start": v(-822.49, 2143.07) * mm, "end": v(-822.49, 4670.91) * mm});
            skLineSegment(sketch, "E158", {"start": v(-822.49, 4670.91) * mm, "end": v(-126.84, 4670.91) * mm});
            skLineSegment(sketch, "E159", {"start": v(2693.07, 1186.1) * mm, "end": v(2693.07, 195.2) * mm});
            skLineSegment(sketch, "E160", {"start": v(2693.07, 195.2) * mm, "end": v(2401.83, 195.2) * mm});
            skLineSegment(sketch, "E161", {"start": v(2401.83, 195.2) * mm, "end": v(2401.83, -482.62) * mm});
            skLineSegment(sketch, "E162", {"start": v(2401.83, -482.62) * mm, "end": v(2693.07, -482.62) * mm});
            skLineSegment(sketch, "E163", {"start": v(2693.07, -482.62) * mm, "end": v(2693.07, -1476.11) * mm});
            skLineSegment(sketch, "E164", {"start": v(2693.07, -1476.11) * mm, "end": v(1975.26, -1476.11) * mm});
            skLineSegment(sketch, "E165", {"start": v(1975.26, -1476.11) * mm, "end": v(1975.26, -1665.17) * mm});
            skLineSegment(sketch, "E166", {"start": v(1975.26, -1665.17) * mm, "end": v(1562.67, -2158.8) * mm});
            skLineSegment(sketch, "E167", {"start": v(1562.67, -2158.8) * mm, "end": v(-117.15, -2158.8) * mm});
            skLineSegment(sketch, "E168", {"start": v(-117.15, -2158.8) * mm, "end": v(-492.9, -1724.11) * mm});
            skLineSegment(sketch, "E169", {"start": v(-492.9, -1724.11) * mm, "end": v(-684.46, -1724.11) * mm});
            skLineSegment(sketch, "E170", {"start": v(-684.46, -1724.11) * mm, "end": v(-684.46, 436.6) * mm});
            skLineSegment(sketch, "E171", {"start": v(-684.46, 1186.1) * mm, "end": v(2693.07, 1186.1) * mm});
            skLineSegment(sketch, "E172.bottom", {"start": v(-670.17, 4522.86) * mm, "end": v(2693.07, 4522.86) * mm});
            skLineSegment(sketch, "E172.top", {"start": v(-670.17, 1354.77) * mm, "end": v(2693.07, 1354.77) * mm});
            skLineSegment(sketch, "E172.left", {"start": v(-670.17, 4522.86) * mm, "end": v(-670.17, 2143.07) * mm});
            skLineSegment(sketch, "E172.right", {"start": v(2693.07, 4522.86) * mm, "end": v(2693.07, 1354.77) * mm});
            skLineSegment(sketch, "E173.bottom", {"start": v(-4234.93, 8205.98) * mm, "end": v(-235.95, 8205.98) * mm});
            skLineSegment(sketch, "E173.top", {"start": v(-4234.93, 4840.18) * mm, "end": v(-235.95, 4840.18) * mm});
            skLineSegment(sketch, "E173.left", {"start": v(-4234.93, 8205.98) * mm, "end": v(-4234.93, 4840.18) * mm});
            skLineSegment(sketch, "E173.right", {"start": v(-235.95, 8205.98) * mm, "end": v(-235.95, 4840.18) * mm});
            skLineSegment(sketch, "E174.bottom", {"start": v(-822.49, 4670.91) * mm, "end": v(-1586.75, 4670.91) * mm});
            skLineSegment(sketch, "E174.left", {"start": v(-822.49, 4670.91) * mm, "end": v(-822.49, 2143.07) * mm});
            skLineSegment(sketch, "E174.right", {"start": v(-4234.93, 4670.91) * mm, "end": v(-4234.93, 402.37) * mm});
            skLineSegment(sketch, "E175", {"start": v(-2883.91, -1724.11) * mm, "end": v(-822.49, -1724.11) * mm});
            skLineSegment(sketch, "E176.bottom", {"start": v(-822.49, -1724.11) * mm, "end": v(-2883.91, -1724.11) * mm});
            skLineSegment(sketch, "E176.left", {"start": v(-822.49, -1724.11) * mm, "end": v(-822.49, 402.37) * mm});
            skLineSegment(sketch, "E176.right", {"start": v(-2948.68, -1724.11) * mm, "end": v(-2948.68, 319.79) * mm});
            skLineSegment(sketch, "E177.bottom", {"start": v(-2883.91, 319.79) * mm, "end": v(-1595.93, 319.79) * mm});
            skLineSegment(sketch, "E177.left", {"start": v(-2883.91, 319.79) * mm, "end": v(-2883.91, -1724.11) * mm});
            skLineSegment(sketch, "E177.right", {"start": v(-822.49, 319.79) * mm, "end": v(-822.49, -1724.11) * mm});
            skLineSegment(sketch, "E178", {"start": v(-684.46, 436.6) * mm, "end": v(-822.49, 436.6) * mm});
            skLineSegment(sketch, "E179", {"start": v(-684.46, 1186.6) * mm, "end": v(-822.49, 1186.6) * mm});
            skLineSegment(sketch, "E180", {"start": v(-670.17, 1393.07) * mm, "end": v(-822.49, 1393.07) * mm});
            skLineSegment(sketch, "E181", {"start": v(-822.49, 1393.07) * mm, "end": v(-822.49, 1403.85) * mm});
            skLineSegment(sketch, "E182", {"start": v(-822.49, 2143.07) * mm, "end": v(-670.17, 2143.07) * mm});
            skLineSegment(sketch, "E183.trimOffspring", {"start": v(-822.49, 1186.6) * mm, "end": v(-822.49, 1403.85) * mm});
            skLineSegment(sketch, "E184.trimOffspring", {"start": v(-684.46, 1186.1) * mm, "end": v(-684.46, 1186.6) * mm});
            skLineSegment(sketch, "E185.trimOffspring", {"start": v(-822.49, 436.6) * mm, "end": v(-822.49, -1529.24) * mm});
            skLineSegment(sketch, "E186.trimOffspring", {"start": v(-670.17, 1393.07) * mm, "end": v(-670.17, 1354.77) * mm});
            skLineSegment(sketch, "E187.trimOffspring", {"start": v(-822.49, 1403.85) * mm, "end": v(-822.49, 1186.6) * mm});
            skLineSegment(sketch, "E188", {"start": v(-1595.93, 402.37) * mm, "end": v(-1595.93, 319.79) * mm});
            skLineSegment(sketch, "E189", {"start": v(-1586.75, 2143.07) * mm, "end": v(-2883.91, 2143.07) * mm});
            skLineSegment(sketch, "E190", {"start": v(-2883.91, 2143.07) * mm, "end": v(-2883.91, 402.37) * mm});
            skLineSegment(sketch, "E191", {"start": v(-2948.68, 402.37) * mm, "end": v(-2948.68, 2143.07) * mm});
            skLineSegment(sketch, "E192", {"start": v(-2948.68, 2300.98) * mm, "end": v(-1714.89, 2300.98) * mm});
            skLineSegment(sketch, "E193", {"start": v(-1586.75, 2143.07) * mm, "end": v(-1586.75, 2300.98) * mm});
            skLineSegment(sketch, "E194", {"start": v(-2883.91, 402.37) * mm, "end": v(-1595.93, 402.37) * mm});
            skLineSegment(sketch, "E195.bottom", {"start": v(-2948.68, 402.37) * mm, "end": v(-4234.93, 402.37) * mm});
            skLineSegment(sketch, "E195.left", {"start": v(-2948.68, 319.79) * mm, "end": v(-2948.68, -1674.58) * mm});
            skLineSegment(sketch, "E195.right", {"start": v(-4347.6, 402.37) * mm, "end": v(-4347.6, 319.79) * mm});
            skLineSegment(sketch, "E196", {"start": v(-2606.46, 319.79) * mm, "end": v(-2883.91, 319.79) * mm});
            skLineSegment(sketch, "E197", {"start": v(-2948.68, -1024.32) * mm, "end": v(-2948.68, -1840.1) * mm});
            skLineSegment(sketch, "E198.trimOffspring", {"start": v(-2948.68, 319.79) * mm, "end": v(-4347.6, 319.79) * mm});
            skLineSegment(sketch, "E199", {"start": v(-1586.75, 2143.07) * mm, "end": v(-1586.75, 2448.43) * mm});
            skLineSegment(sketch, "E200", {"start": v(-1714.89, 4670.91) * mm, "end": v(-1714.89, 4412.16) * mm});
            skLineSegment(sketch, "E201", {"start": v(-1714.89, 2300.98) * mm, "end": v(-3271.59, 2300.98) * mm});
            skLineSegment(sketch, "E202", {"start": v(-4234.93, 2300.98) * mm, "end": v(-4234.93, 2143.07) * mm});
            skLineSegment(sketch, "E203", {"start": v(-4234.93, 2143.07) * mm, "end": v(-4021.59, 2143.07) * mm});
            skLineSegment(sketch, "E204.left", {"start": v(-4021.59, 2300.98) * mm, "end": v(-4021.59, 2143.07) * mm});
            skLineSegment(sketch, "E204.right", {"start": v(-3271.59, 2300.98) * mm, "end": v(-3271.59, 2143.07) * mm});
            skLineSegment(sketch, "E205.trimOffspring", {"start": v(-3271.59, 2143.07) * mm, "end": v(-2948.68, 2143.07) * mm});
            skLineSegment(sketch, "E206.trimOffspring", {"start": v(-4021.59, 2300.98) * mm, "end": v(-4234.93, 2300.98) * mm});
            skLineSegment(sketch, "E207.bottom", {"start": v(-4234.93, 4670.91) * mm, "end": v(-2934.93, 4670.91) * mm});
            skLineSegment(sketch, "E207.left", {"start": v(-4234.93, 4670.91) * mm, "end": v(-4234.93, 2770.91) * mm});
            skLineSegment(sketch, "E207.right", {"start": v(-2934.93, 2770.91) * mm, "end": v(-2934.93, 2751.12) * mm});
            skLineSegment(sketch, "E208.bottom", {"start": v(-3814.24, 4670.91) * mm, "end": v(-2464.24, 4670.91) * mm});
            skLineSegment(sketch, "E208.top", {"start": v(-3814.24, 2770.91) * mm, "end": v(-2464.24, 2770.91) * mm});
            skLineSegment(sketch, "E208.left", {"start": v(-3814.24, 4670.91) * mm, "end": v(-3814.24, 2770.91) * mm});
            skLineSegment(sketch, "E208.right", {"start": v(-2464.24, 4670.91) * mm, "end": v(-2464.24, 2770.91) * mm});
            skLineSegment(sketch, "E209", {"start": v(-2464.24, 2770.91) * mm, "end": v(-3814.24, 2770.91) * mm});
            skLineSegment(sketch, "E210.top", {"start": v(-2464.24, 4670.91) * mm, "end": v(-3814.24, 4670.91) * mm});
            skLineSegment(sketch, "E210.left", {"start": v(-2464.24, 2770.91) * mm, "end": v(-2464.24, 4670.91) * mm});
            skLineSegment(sketch, "E210.right", {"start": v(-3814.24, 2770.91) * mm, "end": v(-3814.24, 4670.91) * mm});
            skLineSegment(sketch, "E211.trimOffspring", {"start": v(-1714.89, 3661.58) * mm, "end": v(-1714.89, 3198.43) * mm});
            skLineSegment(sketch, "E212.trimOffspring", {"start": v(-1586.75, 4412.16) * mm, "end": v(-1586.75, 4670.91) * mm});
            skLineSegment(sketch, "E213.bottom", {"start": v(-1714.89, 2448.43) * mm, "end": v(-1586.75, 2448.43) * mm});
            skLineSegment(sketch, "E213.top", {"start": v(-1714.89, 3198.43) * mm, "end": v(-1586.75, 3198.43) * mm});
            skLineSegment(sketch, "E214.left", {"start": v(-1714.89, 3661.58) * mm, "end": v(-1714.89, 4412.16) * mm});
            skLineSegment(sketch, "E214.right", {"start": v(-1586.75, 3661.58) * mm, "end": v(-1586.75, 4412.16) * mm});
            skLineSegment(sketch, "E215.trimOffspring", {"start": v(-1714.89, 2448.43) * mm, "end": v(-1714.89, 2300.98) * mm});
            skLineSegment(sketch, "E216.trimOffspring", {"start": v(-1586.75, 3198.43) * mm, "end": v(-1586.75, 3661.58) * mm});
            skLineSegment(sketch, "E217.trimOffspring", {"start": v(-1714.89, 4670.91) * mm, "end": v(-4234.93, 4670.91) * mm});
            skSolve(sketch);
        }
        {
            var Q0;
            Q0 = qSketchRegion(id + "F17", true);
            extrude(context, id + "F18", {"entities" : qUnion([Q0]), "operationType" : NewBodyOperationType.ADD, "depth" : 2400 * mm});
        }
        {
            var Q0;
            Q0=makeQuery(id+"F18.boolean.opBoolean","SPLIT",FACE,{"disambiguationData":[TD([makeQuery(id+"F16.boolean.opBoolean","COPY",FACE,{"derivedFrom":makeQuery(id+"F16.opExtrude","SWEPT_FACE",FACE,{"disambiguationData":[OSD([sQuery(id+"F15.wireOp",EDGE,"E140.bottom")])]})})])],"derivedFrom":makeQuery(id+"F14.opExtrude","CAP_FACE",FACE,{"disambiguationData":[OSD([sQuery(id+"F13.wireOp",EDGE,"E128"),sQuery(id+"F13.wireOp",EDGE,"E129"),sQuery(id+"F13.wireOp",EDGE,"E130"),sQuery(id+"F13.wireOp",EDGE,"E131"),sQuery(id+"F13.wireOp",EDGE,"E132"),sQuery(id+"F13.wireOp",EDGE,"E133"),sQuery(id+"F13.wireOp",EDGE,"E134"),sQuery(id+"F13.wireOp",EDGE,"E135"),sQuery(id+"F13.wireOp",EDGE,"E136"),sQuery(id+"F13.wireOp",EDGE,"E137"),sQuery(id+"F13.wireOp",EDGE,"E138"),sQuery(id+"F13.wireOp",EDGE,"E139")])],"isStart":false})});
            var sketch = newSketch(context, id + "F19", { "sketchPlane" : qUnion([Q0])});
            skLineSegment(sketch, "E218.bottom", {"start": v(-3647.84, 4670.91) * mm, "end": v(-2243.86, 4670.91) * mm});
            skLineSegment(sketch, "E218.top", {"start": v(-3647.84, 2770.91) * mm, "end": v(-2243.86, 2770.91) * mm});
            skLineSegment(sketch, "E218.left", {"start": v(-3647.84, 4670.91) * mm, "end": v(-3647.84, 2770.91) * mm});
            skLineSegment(sketch, "E218.right", {"start": v(-2243.86, 4670.91) * mm, "end": v(-2243.86, 2770.91) * mm});
            skSolve(sketch);
        }
        {
            var Q0;
            Q0 = qSketchRegion(id + "F19", true);
            extrude(context, id + "F20", {"entities" : qUnion([Q0]), "operationType" : NewBodyOperationType.ADD, "depth" : 700 * mm});
        }
        {
            var Q0;
            Q0=makeQuery(id+"F18.opExtrude","CAP_FACE",FACE,{"disambiguationData":[OSD([sQuery(id+"F17.wireOp",EDGE,"E144"),sQuery(id+"F17.wireOp",EDGE,"E145"),sQuery(id+"F17.wireOp",EDGE,"E146"),sQuery(id+"F17.wireOp",EDGE,"E147"),sQuery(id+"F17.wireOp",EDGE,"E148"),sQuery(id+"F17.wireOp",EDGE,"E149"),sQuery(id+"F17.wireOp",EDGE,"E150"),sQuery(id+"F17.wireOp",EDGE,"E151"),sQuery(id+"F17.wireOp",EDGE,"E152"),sQuery(id+"F17.wireOp",EDGE,"E153"),sQuery(id+"F17.wireOp",EDGE,"E159"),sQuery(id+"F17.wireOp",EDGE,"E160"),sQuery(id+"F17.wireOp",EDGE,"E161"),sQuery(id+"F17.wireOp",EDGE,"E162"),sQuery(id+"F17.wireOp",EDGE,"E163"),sQuery(id+"F17.wireOp",EDGE,"E164"),sQuery(id+"F17.wireOp",EDGE,"E165"),sQuery(id+"F17.wireOp",EDGE,"E166"),sQuery(id+"F17.wireOp",EDGE,"E167"),sQuery(id+"F17.wireOp",EDGE,"E168"),sQuery(id+"F17.wireOp",EDGE,"E169"),sQuery(id+"F17.wireOp",EDGE,"E170"),sQuery(id+"F17.wireOp",EDGE,"E171"),sQuery(id+"F17.wireOp",EDGE,"E172.bottom"),sQuery(id+"F17.wireOp",EDGE,"E172.top"),sQuery(id+"F17.wireOp",EDGE,"E172.left"),sQuery(id+"F17.wireOp",EDGE,"E172.right"),sQuery(id+"F17.wireOp",EDGE,"E173.bottom"),sQuery(id+"F17.wireOp",EDGE,"E173.top"),sQuery(id+"F17.wireOp",EDGE,"E173.left"),sQuery(id+"F17.wireOp",EDGE,"E173.right"),sQuery(id+"F17.wireOp",EDGE,"E174.bottom"),sQuery(id+"F17.wireOp",EDGE,"E174.left"),sQuery(id+"F17.wireOp",EDGE,"E174.right"),sQuery(id+"F17.wireOp",EDGE,"E177.bottom"),sQuery(id+"F17.wireOp",EDGE,"E175"),sQuery(id+"F17.wireOp",EDGE,"E177.left"),sQuery(id+"F17.wireOp",EDGE,"E177.right"),sQuery(id+"F17.wireOp",EDGE,"E178"),sQuery(id+"F17.wireOp",EDGE,"E179"),sQuery(id+"F17.wireOp",EDGE,"E180"),sQuery(id+"F17.wireOp",EDGE,"E182"),sQuery(id+"F17.wireOp",EDGE,"E184.trimOffspring"),sQuery(id+"F17.wireOp",EDGE,"E185.trimOffspring"),sQuery(id+"F17.wireOp",EDGE,"E186.trimOffspring"),sQuery(id+"F17.wireOp",EDGE,"E187.trimOffspring"),sQuery(id+"F17.wireOp",EDGE,"E188"),sQuery(id+"F17.wireOp",EDGE,"E189"),sQuery(id+"F17.wireOp",EDGE,"E190"),sQuery(id+"F17.wireOp",EDGE,"E191"),sQuery(id+"F17.wireOp",EDGE,"E194"),sQuery(id+"F17.wireOp",EDGE,"E195.bottom"),sQuery(id+"F17.wireOp",EDGE,"E195.left"),sQuery(id+"F17.wireOp",EDGE,"E195.right"),sQuery(id+"F17.wireOp",EDGE,"E196"),sQuery(id+"F17.wireOp",EDGE,"E197"),sQuery(id+"F17.wireOp",EDGE,"E198.trimOffspring"),sQuery(id+"F17.wireOp",EDGE,"E199"),sQuery(id+"F17.wireOp",EDGE,"E200"),sQuery(id+"F17.wireOp",EDGE,"E201"),sQuery(id+"F17.wireOp",EDGE,"E202"),sQuery(id+"F17.wireOp",EDGE,"E204.right"),sQuery(id+"F17.wireOp",EDGE,"E205.trimOffspring"),sQuery(id+"F17.wireOp",EDGE,"E207.left"),sQuery(id+"F17.wireOp",EDGE,"E211.trimOffspring"),sQuery(id+"F17.wireOp",EDGE,"E212.trimOffspring"),sQuery(id+"F17.wireOp",EDGE,"E213.bottom"),sQuery(id+"F17.wireOp",EDGE,"E213.top"),sQuery(id+"F17.wireOp",EDGE,"E214.left"),sQuery(id+"F17.wireOp",EDGE,"E214.right"),sQuery(id+"F17.wireOp",EDGE,"E215.trimOffspring"),sQuery(id+"F17.wireOp",EDGE,"E216.trimOffspring"),sQuery(id+"F17.wireOp",EDGE,"E217.trimOffspring")])],"isStart":false});
            var sketch = newSketch(context, id + "F21", { "sketchPlane" : qUnion([Q0])});
            skLineSegment(sketch, "E219.bottom", {"start": v(-2948.68, 4670.91) * mm, "end": v(2812.4, 4670.91) * mm});
            skLineSegment(sketch, "E219.top", {"start": v(-2948.68, -1840.1) * mm, "end": v(2812.4, -1840.1) * mm});
            skLineSegment(sketch, "E219.left", {"start": v(-2948.68, 319.79) * mm, "end": v(-2948.68, -1840.1) * mm});
            skLineSegment(sketch, "E219.right", {"start": v(2812.4, 4670.91) * mm, "end": v(2812.4, -1840.1) * mm});
            skLineSegment(sketch, "E220.bottom", {"start": v(-2948.68, 4670.91) * mm, "end": v(-4347.6, 4670.91) * mm});
            skLineSegment(sketch, "E220.top", {"start": v(-2948.68, 319.79) * mm, "end": v(-4347.6, 319.79) * mm});
            skLineSegment(sketch, "E220.right", {"start": v(-4347.6, 4670.91) * mm, "end": v(-4347.6, 319.79) * mm});
            skSolve(sketch);
        }
        {
            var Q0;
            Q0 = qSketchRegion(id + "F21", true);
            extrude(context, id + "F22", {"entities" : qUnion([Q0]), "depth" : 2400 * mm});
        }
        {
            var Q0;
            Q0=makeQuery(id+"F22.opExtrude","SWEPT_FACE",FACE,{"disambiguationData":[OSD([sQuery(id+"F21.wireOp",EDGE,"E219.right")])]});
            var sketch = newSketch(context, id + "F23", { "sketchPlane" : qUnion([Q0])});
            skLineSegment(sketch, "E221", {"start": v(-1840.1, 5010) * mm, "end": v(1415.41, 7410) * mm});
            skLineSegment(sketch, "E222", {"start": v(1415.41, 7410) * mm, "end": v(4670.91, 5010) * mm});
            skSolve(sketch);
        }
        {
            var Q0;
            {var subQ2=sQuery(id+"F23.wireOp",EDGE,"E221");Q0=makeQuery(id+"F23.imprint","IMPRINT",FACE,{"disambiguationData":[TD([[makeQuery(id+"F23.imprint","IMPRINT",EDGE,{"derivedFrom":subQ2}),1.0]])]});}
            var Q1;
            {var subQ2=sQuery(id+"F23.wireOp",EDGE,"E222");Q1=makeQuery(id+"F23.imprint","IMPRINT",FACE,{"disambiguationData":[TD([[makeQuery(id+"F23.imprint","IMPRINT",EDGE,{"derivedFrom":subQ2}),1.0]])]});}
            extrude(context, id + "F24", {"entities" : qUnion([Q0, Q1]), "operationType" : NewBodyOperationType.REMOVE, "endBound" : BoundingType.THROUGH_ALL, "oppositeDirection" : true, "depth" : 25 * mm});
        }
        {
            var Q0;
            Q0=makeQuery(id+"F18.boolean.opBoolean","MERGE",FACE,{"derivedFrom":[makeQuery(id+"F14.opExtrude","SWEPT_FACE",FACE,{"disambiguationData":[OSD([sQuery(id+"F13.wireOp",EDGE,"E132")])]}),makeQuery(id+"F18.opExtrude","SWEPT_FACE",FACE,{"disambiguationData":[OSD([sQuery(id+"F17.wireOp",EDGE,"E151")])]})]});
            var sketch = newSketch(context, id + "F25", { "sketchPlane" : qUnion([Q0])});
            skLineSegment(sketch, "E223", {"start": v(-2948.68, 5010) * mm, "end": v(780.24, 7583.78) * mm});
            skLineSegment(sketch, "E224", {"start": v(780.24, 7583.78) * mm, "end": v(-5054.69, 7583.78) * mm});
            skLineSegment(sketch, "E225.bottom", {"start": v(-2948.68, 5010) * mm, "end": v(-5054.69, 5010) * mm});
            skLineSegment(sketch, "E225.top", {"start": v(-2948.68, 7583.78) * mm, "end": v(-5054.69, 7583.78) * mm});
            skLineSegment(sketch, "E225.right", {"start": v(-5054.69, 5010) * mm, "end": v(-5054.69, 7583.78) * mm});
            skSolve(sketch);
        }
        {
            var Q0;
            Q0 = qSketchRegion(id + "F25", true);
            extrude(context, id + "F26", {"entities" : qUnion([Q0]), "operationType" : NewBodyOperationType.REMOVE, "endBound" : BoundingType.THROUGH_ALL, "oppositeDirection" : true, "depth" : 25 * mm});
        }
        {
            var Q0;
            Q0=makeQuery(id+"F18.boolean.opBoolean","MERGE",FACE,{"derivedFrom":[makeQuery(id+"F14.opExtrude","SWEPT_FACE",FACE,{"disambiguationData":[OSD([sQuery(id+"F13.wireOp",EDGE,"E134")])]}),makeQuery(id+"F18.opExtrude","SWEPT_FACE",FACE,{"disambiguationData":[OSD([sQuery(id+"F17.wireOp",EDGE,"E149")])]})]});
            var sketch = newSketch(context, id + "F27", { "sketchPlane" : qUnion([Q0])});
            skLineSegment(sketch, "E226.bottom", {"start": v(1478.97, 4298.86) * mm, "end": v(-74.9, 4298.86) * mm});
            skLineSegment(sketch, "E226.top", {"start": v(1478.97, 3417.35) * mm, "end": v(-74.9, 3417.35) * mm});
            skLineSegment(sketch, "E226.left", {"start": v(1478.97, 4298.86) * mm, "end": v(1478.97, 3417.35) * mm});
            skLineSegment(sketch, "E226.right", {"start": v(-74.9, 4298.86) * mm, "end": v(-74.9, 3417.35) * mm});
            skLineSegment(sketch, "E227.bottom", {"start": v(-74.9, 4645.18) * mm, "end": v(1478.97, 4645.18) * mm});
            skLineSegment(sketch, "E227.top", {"start": v(-74.9, 4381.45) * mm, "end": v(1478.97, 4381.45) * mm});
            skLineSegment(sketch, "E227.left", {"start": v(-74.9, 4645.18) * mm, "end": v(-74.9, 4381.45) * mm});
            skLineSegment(sketch, "E227.right", {"start": v(1478.97, 4645.18) * mm, "end": v(1478.97, 4381.45) * mm});
            skLineSegment(sketch, "E228", {"start": v(702.03, 4645.18) * mm, "end": v(702.03, 4381.45) * mm});
            skSolve(sketch);
        }
        {
            var Q0;
            Q0 = qSketchRegion(id + "F27", true);
            extrude(context, id + "F28", {"entities" : qUnion([Q0]), "operationType" : NewBodyOperationType.REMOVE, "endBound" : BoundingType.UP_TO_NEXT, "oppositeDirection" : true, "depth" : 25 * mm});
        }
        {
            var Q0;
            Q0=makeQuery(id+"F18.opExtrude","SWEPT_FACE",FACE,{"disambiguationData":[OSD([sQuery(id+"F17.wireOp",EDGE,"E195.left"),sQuery(id+"F17.wireOp",EDGE,"E197")])]});
            var sketch = newSketch(context, id + "F29", { "sketchPlane" : qUnion([Q0])});
            skLineSegment(sketch, "E229.bottom", {"start": v(-150.17, 3958.84) * mm, "end": v(355.16, 3958.84) * mm});
            skLineSegment(sketch, "E229.top", {"start": v(-150.17, 4592.22) * mm, "end": v(355.16, 4592.22) * mm});
            skLineSegment(sketch, "E229.left", {"start": v(-150.17, 3958.84) * mm, "end": v(-150.17, 4592.22) * mm});
            skLineSegment(sketch, "E229.right", {"start": v(355.16, 3958.84) * mm, "end": v(355.16, 4592.22) * mm});
            skSolve(sketch);
        }
        {
            var Q0;
            Q0=makeQuery(id+"F29.imprint","IMPRINT",FACE,{"disambiguationData":[TD([[makeQuery(id+"F29.imprint","IMPRINT",EDGE,{"derivedFrom":sQuery(id+"F29.wireOp",EDGE,"E229.bottom")}),1.0]])]});
            extrude(context, id + "F30", {"entities" : qUnion([Q0]), "operationType" : NewBodyOperationType.REMOVE, "endBound" : BoundingType.UP_TO_NEXT, "oppositeDirection" : true, "depth" : 25 * mm});
        }
        {
            var Q0;
            Q0=makeQuery(id+"F18.boolean.opBoolean","MERGE",FACE,{"derivedFrom":[makeQuery(id+"F14.opExtrude","SWEPT_FACE",FACE,{"disambiguationData":[OSD([sQuery(id+"F13.wireOp",EDGE,"E132")])]}),makeQuery(id+"F18.opExtrude","SWEPT_FACE",FACE,{"disambiguationData":[OSD([sQuery(id+"F17.wireOp",EDGE,"E151")])]})]});
            var sketch = newSketch(context, id + "F31", { "sketchPlane" : qUnion([Q0])});
            skLineSegment(sketch, "E230", {"start": v(-2948.68, 5010) * mm, "end": v(-5369.5, 3339.1) * mm});
            skLineSegment(sketch, "E231", {"start": v(-5369.5, 3339.1) * mm, "end": v(-5369.5, 10103.4) * mm});
            skLineSegment(sketch, "E232", {"start": v(-5369.5, 10103.4) * mm, "end": v(-2948.68, 5010) * mm});
            skSolve(sketch);
        }
        {
            var Q0;
            Q0=makeQuery(id+"F31.imprint","IMPRINT",FACE,{"disambiguationData":[TD([[makeQuery(id+"F31.imprint","IMPRINT",EDGE,{"derivedFrom":sQuery(id+"F31.wireOp",EDGE,"E230")}),-1.0]])]});
            extrude(context, id + "F32", {"entities" : qUnion([Q0]), "operationType" : NewBodyOperationType.REMOVE, "endBound" : BoundingType.THROUGH_ALL, "oppositeDirection" : true, "depth" : 25 * mm});
        }
        {
            var Q0;
            Q0=makeQuery(id+"F18.boolean.opBoolean","MERGE",FACE,{"derivedFrom":[makeQuery(id+"F14.opExtrude","SWEPT_FACE",FACE,{"disambiguationData":[OSD([sQuery(id+"F13.wireOp",EDGE,"E132")])]}),makeQuery(id+"F18.opExtrude","SWEPT_FACE",FACE,{"disambiguationData":[OSD([sQuery(id+"F17.wireOp",EDGE,"E151")])]})]});
            var sketch = newSketch(context, id + "F33", { "sketchPlane" : qUnion([Q0])});
            skLineSegment(sketch, "E233.bottom", {"start": v(-2536.64, 4645.18) * mm, "end": v(-959.93, 4645.18) * mm});
            skLineSegment(sketch, "E233.top", {"start": v(-2536.64, 3417.35) * mm, "end": v(-959.93, 3417.35) * mm});
            skLineSegment(sketch, "E233.left", {"start": v(-2536.64, 4645.18) * mm, "end": v(-2536.64, 3417.35) * mm});
            skLineSegment(sketch, "E233.right", {"start": v(-959.93, 4645.18) * mm, "end": v(-959.93, 3417.35) * mm});
            skSolve(sketch);
        }
        {
            var Q0;
            Q0=makeQuery(id+"F33.imprint","IMPRINT",FACE,{"disambiguationData":[TD([[makeQuery(id+"F33.imprint","IMPRINT",EDGE,{"derivedFrom":sQuery(id+"F33.wireOp",EDGE,"E233.bottom")}),-1.0]])]});
            var Q1;
            Q1=makeQuery(id+"F33.imprint","IMPRINT",FACE,{"disambiguationData":[TD([[makeQuery(id+"F33.imprint","IMPRINT",EDGE,{"derivedFrom":sQuery(id+"F33.wireOp",EDGE,"7aa86f14-0b1e-4f1a-9f1a-8a8825f2f83e.bottom")}),-1.0]])]});
            extrude(context, id + "F34", {"entities" : qUnion([Q0, Q1]), "operationType" : NewBodyOperationType.REMOVE, "oppositeDirection" : true, "depth" : 468.7 * mm});
        }
        {
            var Q0;
            Q0=makeQuery(id+"F18.boolean.opBoolean","MERGE",FACE,{"derivedFrom":[makeQuery(id+"F14.opExtrude","SWEPT_FACE",FACE,{"disambiguationData":[OSD([sQuery(id+"F13.wireOp",EDGE,"E132")])]}),makeQuery(id+"F18.opExtrude","SWEPT_FACE",FACE,{"disambiguationData":[OSD([sQuery(id+"F17.wireOp",EDGE,"E151")])]})]});
            var sketch = newSketch(context, id + "F35", { "sketchPlane" : qUnion([Q0])});
            skLineSegment(sketch, "E234", {"start": v(-4991.66, 4290.1) * mm, "end": v(-219.76, 7583.78) * mm});
            skLineSegment(sketch, "E235", {"start": v(-219.76, 7583.78) * mm, "end": v(-3921.3, 7583.78) * mm});
            skLineSegment(sketch, "E236", {"start": v(-3921.3, 7583.78) * mm, "end": v(-4991.66, 4290.1) * mm});
            skSolve(sketch);
        }
        {
            var Q0;
            Q0=makeQuery(id+"F35.imprint","IMPRINT",FACE,{"disambiguationData":[TD([[makeQuery(id+"F35.imprint","IMPRINT",EDGE,{"derivedFrom":sQuery(id+"F35.wireOp",EDGE,"E234")}),1.0]])]});
            extrude(context, id + "F36", {"entities" : qUnion([Q0]), "operationType" : NewBodyOperationType.REMOVE, "oppositeDirection" : true, "depth" : 12162.87 * mm});
        }
        {
            var Q0;
            Q0=makeQuery(id+"F18.opExtrude","SWEPT_FACE",FACE,{"disambiguationData":[OSD([sQuery(id+"F17.wireOp",EDGE,"E198.trimOffspring")])]});
            var sketch = newSketch(context, id + "F37", { "sketchPlane" : qUnion([Q0])});
            skLineSegment(sketch, "E237", {"start": v(-4347.6, 2610) * mm, "end": v(-2948.68, 3575.56) * mm});
            skLineSegment(sketch, "E238", {"start": v(-2948.68, 3575.56) * mm, "end": v(-2948.68, 2610) * mm});
            skLineSegment(sketch, "E239", {"start": v(-2948.68, 2610) * mm, "end": v(-4347.6, 2610) * mm});
            skSolve(sketch);
        }
        {
            var Q0;
            Q0=makeQuery(id+"F37.imprint","IMPRINT",FACE,{"disambiguationData":[TD([[makeQuery(id+"F37.imprint","IMPRINT",EDGE,{"derivedFrom":sQuery(id+"F37.wireOp",EDGE,"E237")}),-1.0]])]});
            var Q1;
            Q1=makeQuery(id+"F14.opExtrude","SWEPT_FACE",FACE,{"disambiguationData":[OSD([sQuery(id+"F13.wireOp",EDGE,"E130")])]});
            extrude(context, id + "F38", {"entities" : qUnion([Q0]), "operationType" : NewBodyOperationType.ADD, "endBound" : BoundingType.UP_TO_SURFACE, "endBoundEntityFace" : qUnion([Q1]), "depth" : 1787.5 * mm});
        }
        {
            var Q0;
            Q0=makeQuery(id+"F2.opExtrude","SWEPT_FACE",FACE,{"disambiguationData":[OSD([sQuery(id+"F0.wireOp",EDGE,"E7"),sQuery(id+"F0.wireOp",EDGE,"E85"),sQuery(id+"F0.wireOp",EDGE,"91a161d4-26f4-4b8d-b4cb-e70c712e9d70")])]});
            var sketch = newSketch(context, id + "F39", { "sketchPlane" : qUnion([Q0])});
            skSolve(sketch);
        }
        {
            var Q0;
            {var subQ0=sQuery(id+"F0.wireOp",EDGE,"E7");Q0=makeQuery(id+"F39.imprint","IMPRINT",FACE,{"disambiguationData":[TD([[makeQuery(id+"F39.imprint","IMPRINT",EDGE,{"derivedFrom":makeQuery(id+"F2.opExtrude","SWEPT_EDGE",EDGE,{"disambiguationData":[OSD([subQ0,sQuery(id+"F0.wireOp",EDGE,"E8")])]})}),-1.0]])]});}
            var sketch = newSketch(context, id + "F40", { "sketchPlane" : qUnion([Q0])});
            skLineSegment(sketch, "E240.bottom", {"start": v(353.88, 0) * mm, "end": v(-470.72, 0) * mm});
            skLineSegment(sketch, "E240.top", {"start": v(353.88, 1700.24) * mm, "end": v(-470.72, 1700.24) * mm});
            skLineSegment(sketch, "E240.left", {"start": v(353.88, 0) * mm, "end": v(353.88, 1700.24) * mm});
            skLineSegment(sketch, "E240.right", {"start": v(-470.72, 0) * mm, "end": v(-470.72, 1700.24) * mm});
            skLineSegment(sketch, "E241.bottom", {"start": v(412.5, 2220.14) * mm, "end": v(-550.26, 2220.14) * mm});
            skLineSegment(sketch, "E241.top", {"start": v(412.5, 1903.32) * mm, "end": v(-550.26, 1903.32) * mm});
            skLineSegment(sketch, "E241.left", {"start": v(412.5, 2220.14) * mm, "end": v(412.5, 1903.32) * mm});
            skLineSegment(sketch, "E241.right", {"start": v(-550.26, 2220.14) * mm, "end": v(-550.26, 1903.32) * mm});
            skLineSegment(sketch, "E242.bottom", {"start": v(-699.77, 2220.14) * mm, "end": v(-1444.2, 2220.14) * mm});
            skLineSegment(sketch, "E242.top", {"start": v(-699.77, 1903.32) * mm, "end": v(-1444.2, 1903.32) * mm});
            skLineSegment(sketch, "E242.left", {"start": v(-699.77, 2220.14) * mm, "end": v(-699.77, 1903.32) * mm});
            skLineSegment(sketch, "E242.right", {"start": v(-1444.2, 2220.14) * mm, "end": v(-1444.2, 1903.32) * mm});
            skLineSegment(sketch, "E243.bottom", {"start": v(-1541.38, 2220.14) * mm, "end": v(-2342.93, 2220.14) * mm});
            skLineSegment(sketch, "E243.top", {"start": v(-1541.38, 1903.32) * mm, "end": v(-2342.93, 1903.32) * mm});
            skLineSegment(sketch, "E243.left", {"start": v(-1541.38, 2220.14) * mm, "end": v(-1541.38, 1903.32) * mm});
            skLineSegment(sketch, "E243.right", {"start": v(-2342.93, 2220.14) * mm, "end": v(-2342.93, 1903.32) * mm});
            skSolve(sketch);
        }
        {
            var Q0;
            Q0 = qSketchRegion(id + "F40", true);
            extrude(context, id + "F41", {"entities" : qUnion([Q0]), "operationType" : NewBodyOperationType.REMOVE, "oppositeDirection" : true, "depth" : 433.06 * mm});
        }
        {
            var Q0;
            Q0 = qSketchRegion(id + "F1", true);
            extrude(context, id + "F42", {"entities" : qUnion([Q0]), "depth" : 900 * mm});
        }
    });
